# Revit family: C_E60_19_3-R_2DO_CAD_MULT_Prod
name_source: partatom
category: Detail Items
revit_build: Autodesk Revit 2015 (Build: 20140606_1530(x64)
units: mm (PartAtom-declared; Revit-internal decimal feet)

## types (2) — shared parameters
Density = 0.10 kg
Description = washer
EPD = https://www.strongtie.eu
ETA / DoP = https://www.strongtie.eu
Manufacturer = Simpson Strong-Tie
Model = E60/19/3-R
Model Disclaimer = Contact Simpson Strong-Tie Company  for more information
Model ID = 0238017467224211310235119569792129436967
Name = E60/19/3-R
ObjectType = E60/19/3-R
Product Material = EPDM Compact
Product Type = washer
Reference = E60/19/3-R
Technical datasheet = https://www.strongtie.eu
URL = www.strongtie.eu
UniClass Number = Pr_20_29_31_13
UniClass Title = Carbon steel punched metal plate fasteners

## per-type parameters (varying)
| type | _visiblefront | _visibletop |
| SST_E60/19/3-R_Top | No | Yes |
| SST_E60/19/3-R_Front | Yes | No |

## geometry (parser evidence)
native form markers: Sweep x2
no freeform markers — native parametric forms only
